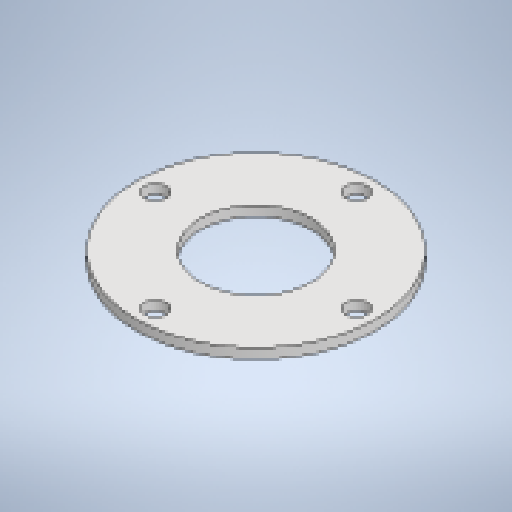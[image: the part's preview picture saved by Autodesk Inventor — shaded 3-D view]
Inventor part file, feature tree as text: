
AUTODESK INVENTOR PART (.ipt)
format: ipt  version: 2025 (Build 290162010, 162A)  size: 194,560 bytes
history: native  units: mm
features: other x3, sketch x2, sheet_metal_op x1, pattern_circular x1
ambient origin geometry x8: Origin, YZ Plane, XZ Plane, XY Plane, X Axis, Y Axis, Z Axis, Center Point
bodies: Body1 (feature_tree)
feature tree (7):
  sheet_metal_op  "Face2"
  pattern_circular  "Circular Pattern1"  [2 undecoded]
  sketch  "Sketch2"  dims[d14=8.0mm]
  other  "Plate2"
  sketch  "Sketch3"  dims[d15=17.0mm d17=8.0mm d18=0.0mm d19=40.0mm d20=360.0deg d25=91.0mm d27=190.0mm d28=160.0mm]
  other  "Cut1"
  other  "Definition1"
note: 2 required parameter values undecoded (feature->parameter linkage not recoverable at this tier; creation-order binding heuristic only, values carry confidence <= 0.55)
